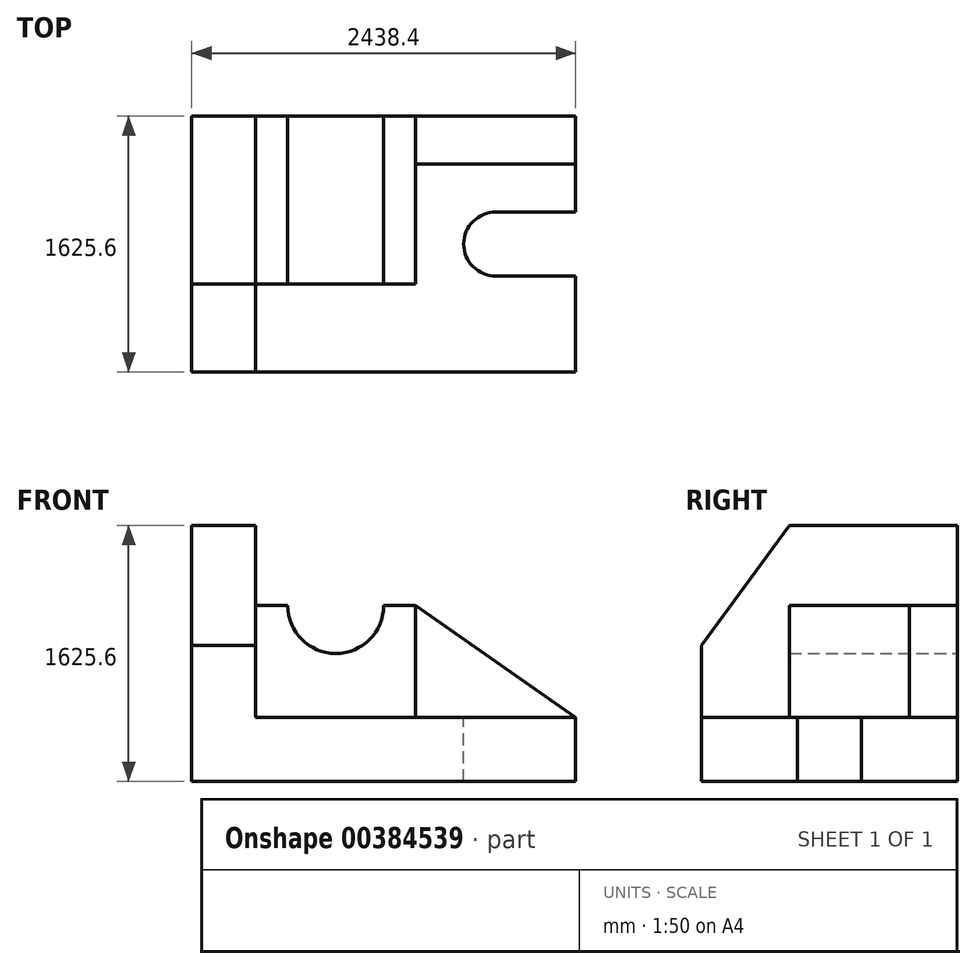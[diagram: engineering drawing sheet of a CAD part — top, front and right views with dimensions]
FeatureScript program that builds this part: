
annotation { "Feature Type Name" : "Feature", "Feature Type Description" : "" }
export const myFeature = defineFeature(function(context is Context, id is Id, definition is map)
    precondition{}
    {
        {
            var Q0;
            Q0=qCreatedBy(makeId("Front.planeOp"),FACE);
            var sketch = newSketch(context, id + "F0", { "sketchPlane" : qUnion([Q0])});
            skLineSegment(sketch, "E0", {"start": v(0, 0) * mm, "end": v(2438.4, 0) * mm});
            skLineSegment(sketch, "E1", {"start": v(2438.4, 0) * mm, "end": v(2438.4, 406.4) * mm});
            skLineSegment(sketch, "E2", {"start": v(2438.4, 406.4) * mm, "end": v(406.4, 406.4) * mm});
            skLineSegment(sketch, "E3", {"start": v(406.4, 406.4) * mm, "end": v(406.4, 1625.6) * mm});
            skLineSegment(sketch, "E4", {"start": v(406.4, 1625.6) * mm, "end": v(0, 1625.6) * mm});
            skLineSegment(sketch, "E5", {"start": v(0, 1625.6) * mm, "end": v(0, 0) * mm});
            skSolve(sketch);
        }
        {
            var Q0;
            Q0=makeQuery(id+"F0.imprint","IMPRINT",FACE,{"disambiguationData":[TD([[makeQuery(id+"F0.imprint","IMPRINT",EDGE,{"derivedFrom":sQuery(id+"F0.wireOp",EDGE,"E0")}),1.0]])]});
            extrude(context, id + "F1", {"entities" : qUnion([Q0]), "depth" : 1625.6 * mm});
        }
        {
            var Q0;
            Q0=makeQuery(id+"F1.opExtrude","SWEPT_FACE",FACE,{"disambiguationData":[OSD([sQuery(id+"F0.wireOp",EDGE,"E2")])]});
            var sketch = newSketch(context, id + "F2", { "sketchPlane" : qUnion([Q0])});
            skLineSegment(sketch, "E6", {"start": v(2438.4, 0) * mm, "end": v(2438.4, -609.6) * mm});
            skLineSegment(sketch, "E7", {"start": v(2438.4, -609.6) * mm, "end": v(2438.4, -1016) * mm});
            skLineSegment(sketch, "E8", {"start": v(2438.4, -1016) * mm, "end": v(2438.4, -1625.6) * mm});
            skLineSegment(sketch, "E9", {"start": v(2438.4, -1016) * mm, "end": v(1930.4, -1016) * mm});
            skLineSegment(sketch, "E10", {"start": v(2438.4, -609.6) * mm, "end": v(1930.4, -609.6) * mm});
            skArc(sketch, "E11", {"start": v(1930.4, -609.6) * mm, "mid": v(1727.2, -812.8) * mm, "end": v(1930.4, -1016) * mm});
            skSolve(sketch);
        }
        {
            var Q0;
            Q0=makeQuery(id+"F2.imprint","IMPRINT",FACE,{"disambiguationData":[TD([[makeQuery(id+"F2.imprint","IMPRINT",EDGE,{"derivedFrom":sQuery(id+"F2.wireOp",EDGE,"E7")}),1.0]])]});
            extrude(context, id + "F3", {"entities" : qUnion([Q0]), "operationType" : NewBodyOperationType.REMOVE, "endBound" : BoundingType.THROUGH_ALL, "oppositeDirection" : true, "depth" : 25.4 * mm});
        }
        {
            var Q0;
            Q0=makeQuery(id+"F1.opExtrude","SWEPT_FACE",FACE,{"disambiguationData":[OSD([sQuery(id+"F0.wireOp",EDGE,"E5")])]});
            var sketch = newSketch(context, id + "F4", { "sketchPlane" : qUnion([Q0])});
            skSolve(sketch);
        }
        {
            var Q0;
            Q0=makeQuery(id+"F1.opExtrude","SWEPT_FACE",FACE,{"disambiguationData":[OSD([sQuery(id+"F0.wireOp",EDGE,"E3")])]});
            var sketch = newSketch(context, id + "F5", { "sketchPlane" : qUnion([Q0])});
            skLineSegment(sketch, "E12", {"start": v(0, 406.4) * mm, "end": v(0, 1117.6) * mm});
            skLineSegment(sketch, "E13", {"start": v(0, 1117.6) * mm, "end": v(-1066.8, 1117.6) * mm});
            skLineSegment(sketch, "E14", {"start": v(-1066.8, 1117.6) * mm, "end": v(-1066.8, 406.4) * mm});
            skLineSegment(sketch, "E15", {"start": v(-1066.8, 406.4) * mm, "end": v(0, 406.4) * mm});
            skSolve(sketch);
        }
        {
            var Q0;
            Q0=makeQuery(id+"F5.imprint","IMPRINT",FACE,{"disambiguationData":[TD([[makeQuery(id+"F5.imprint","IMPRINT",EDGE,{"derivedFrom":sQuery(id+"F5.wireOp",EDGE,"E12")}),1.0]])]});
            extrude(context, id + "F6", {"entities" : qUnion([Q0]), "operationType" : NewBodyOperationType.ADD, "depth" : 1016 * mm});
        }
        {
            var Q0;
            Q0=makeQuery(id+"F6.boolean.opBoolean","MERGE",FACE,{"derivedFrom":[makeQuery(id+"F1.opExtrude","CAP_FACE",FACE,{"disambiguationData":[OSD([sQuery(id+"F0.wireOp",EDGE,"E0"),sQuery(id+"F0.wireOp",EDGE,"E1"),sQuery(id+"F0.wireOp",EDGE,"E2"),sQuery(id+"F0.wireOp",EDGE,"E3"),sQuery(id+"F0.wireOp",EDGE,"E4"),sQuery(id+"F0.wireOp",EDGE,"E5")])],"isStart":true}),makeQuery(id+"F6.opExtrude","SWEPT_FACE",FACE,{"disambiguationData":[OSD([sQuery(id+"F5.wireOp",EDGE,"E12")])]})]});
            var sketch = newSketch(context, id + "F7", { "sketchPlane" : qUnion([Q0])});
            skLineSegment(sketch, "E16", {"start": v(-1422.4, 1117.6) * mm, "end": v(-914.4, 1117.6) * mm});
            skArc(sketch, "E17", {"start": v(-1219.2, 1117.6) * mm, "mid": v(-914.4, 812.8) * mm, "end": v(-609.6, 1117.6) * mm});
            skLineSegment(sketch, "E18", {"start": v(-1422.4, 1117.6) * mm, "end": v(-406.4, 1117.6) * mm});
            skSolve(sketch);
        }
        {
            var Q0;
            {var subQ0=sQuery(id+"F7.wireOp",EDGE,"E17");Q0=makeQuery(id+"F7.imprint","IMPRINT",FACE,{"disambiguationData":[TD([[makeQuery(id+"F7.imprint","IMPRINT",EDGE,{"derivedFrom":subQ0}),1.0]])]});}
            extrude(context, id + "F8", {"entities" : qUnion([Q0]), "operationType" : NewBodyOperationType.REMOVE, "endBound" : BoundingType.THROUGH_ALL, "oppositeDirection" : true, "depth" : 25.4 * mm});
        }
        {
            var Q0;
            Q0=makeQuery(id+"F6.boolean.opBoolean","MERGE",FACE,{"derivedFrom":[makeQuery(id+"F1.opExtrude","CAP_FACE",FACE,{"disambiguationData":[OSD([sQuery(id+"F0.wireOp",EDGE,"E0"),sQuery(id+"F0.wireOp",EDGE,"E1"),sQuery(id+"F0.wireOp",EDGE,"E2"),sQuery(id+"F0.wireOp",EDGE,"E3"),sQuery(id+"F0.wireOp",EDGE,"E4"),sQuery(id+"F0.wireOp",EDGE,"E5")])],"isStart":true}),makeQuery(id+"F6.opExtrude","SWEPT_FACE",FACE,{"disambiguationData":[OSD([sQuery(id+"F5.wireOp",EDGE,"E12")])]})]});
            var sketch = newSketch(context, id + "F9", { "sketchPlane" : qUnion([Q0])});
            skLineSegment(sketch, "E19", {"start": v(-1422.4, 1117.6) * mm, "end": v(-2438.4, 406.4) * mm});
            skLineSegment(sketch, "E20", {"start": v(-1422.4, 1117.6) * mm, "end": v(-1422.4, 406.4) * mm});
            skLineSegment(sketch, "E21", {"start": v(-1422.4, 406.4) * mm, "end": v(-2438.4, 406.4) * mm});
            skSolve(sketch);
        }
        {
            var Q0;
            Q0=makeQuery(id+"F9.imprint","IMPRINT",FACE,{"disambiguationData":[TD([[makeQuery(id+"F9.imprint","IMPRINT",EDGE,{"derivedFrom":sQuery(id+"F9.wireOp",EDGE,"E19")}),1.0]])]});
            extrude(context, id + "F10", {"entities" : qUnion([Q0]), "operationType" : NewBodyOperationType.ADD, "oppositeDirection" : true, "depth" : 304.8 * mm});
        }
        {
            var Q0;
            Q0=makeQuery(id+"F1.opExtrude","SWEPT_FACE",FACE,{"disambiguationData":[OSD([sQuery(id+"F0.wireOp",EDGE,"E3")])]});
            var sketch = newSketch(context, id + "F11", { "sketchPlane" : qUnion([Q0])});
            skLineSegment(sketch, "E22", {"start": v(-1625.6, 406.4) * mm, "end": v(-1625.6, 863.6) * mm});
            skLineSegment(sketch, "E23", {"start": v(-1625.6, 863.6) * mm, "end": v(-1066.8, 863.6) * mm});
            skLineSegment(sketch, "E24", {"start": v(-1066.8, 863.6) * mm, "end": v(-1066.8, 1625.6) * mm});
            skLineSegment(sketch, "E25", {"start": v(-1066.8, 1625.6) * mm, "end": v(-1625.6, 863.6) * mm});
            skSolve(sketch);
        }
        {
            var Q0;
            {var subQ0=sQuery(id+"F11.wireOp",EDGE,"E25");Q0=makeQuery(id+"F11.imprint","IMPRINT",FACE,{"disambiguationData":[TD([[makeQuery(id+"F11.imprint","IMPRINT",EDGE,{"derivedFrom":subQ0}),-1.0]])]});}
            extrude(context, id + "F12", {"entities" : qUnion([Q0]), "operationType" : NewBodyOperationType.REMOVE, "endBound" : BoundingType.THROUGH_ALL, "oppositeDirection" : true, "depth" : 25.4 * mm});
        }
    });
